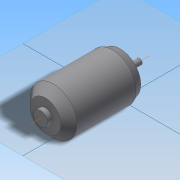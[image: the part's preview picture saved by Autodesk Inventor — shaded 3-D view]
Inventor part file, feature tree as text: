
AUTODESK INVENTOR PART (.ipt)
format: ipt  version: 2014 SP2 (Build 180246200, 246)  size: 108,032 bytes
history: native  units: in
note: dims shown in document units (in); Inventor stores cm internally (conversion verified against a paired STEP export)
features: extrude x3, sketch x3, chamfer x2
ambient origin geometry x8: Origin, YZ Plane, XZ Plane, XY Plane, X Axis, Y Axis, Z Axis, Center Point
bodies: Solid1 (feature_tree)
feature tree (8):
  extrude  "Extrusion1"  Depth=3.2677in TaperAngle=0.0deg
  extrude  "Extrusion2"  Depth=0.7874in TaperAngle=0.0deg
  chamfer  "Chamfer1"  Distance=0.1181in Angle=45.0deg
  extrude  "Extrusion3"  Depth=0.1969in TaperAngle=0.0deg
  chamfer  "Chamfer2"  Distance=0.3311in Angle=45.0deg
  sketch  "Sketch1"  dims[d0=1.9291in d1=3.2677in d2=0.0in]
  sketch  "Sketch2"  dims[d3=0.2362in d4=0.7874in d5=0.0in d7=0.1181in d8=0.315in d9=45.0deg]
  sketch  "Sketch4"  dims[d10=0.5709in d11=0.1969in d12=0.0in d13=0.3311in d14=0.3311in d15=45.0deg]
